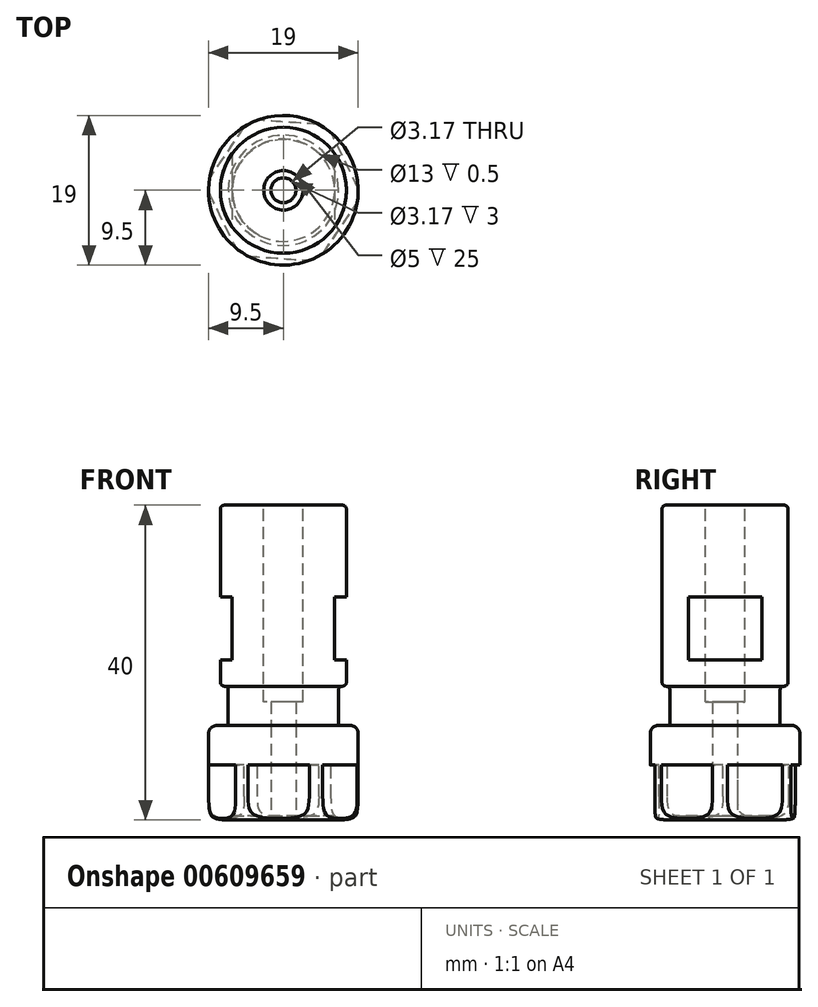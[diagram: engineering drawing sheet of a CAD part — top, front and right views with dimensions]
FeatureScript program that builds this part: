
annotation { "Feature Type Name" : "Feature", "Feature Type Description" : "" }
export const myFeature = defineFeature(function(context is Context, id is Id, definition is map)
    precondition{}
    {
        {
            var Q0;
            Q0=qCreatedBy(makeId("Top.planeOp"),FACE);
            var sketch = newSketch(context, id + "F0", { "sketchPlane" : qUnion([Q0])});
            skCircle(sketch, "E0", {"center": v(0, 0) * mm, "radius": 8 * mm});
            skSolve(sketch);
        }
        {
            var Q0;
            Q0=qSketchRegion(id+"F0",true);
            extrude(context, id + "F1", {"entities" : qUnion([Q0]), "depth" : 28 * mm, "offsetDistance" : 25 * mm});
        }
        {
            var Q0;
            Q0=qCreatedBy(makeId("Top.planeOp"),FACE);
            var sketch = newSketch(context, id + "F2", { "sketchPlane" : qUnion([Q0])});
            skCircle(sketch, "E1", {"center": v(0, 0) * mm, "radius": 7 * mm});
            skCircle(sketch, "E2", {"center": v(0, 0) * mm, "radius": 9.32 * mm});
            skSolve(sketch);
        }
        {
            var Q0;
            Q0=qSketchRegion(id+"F2",true);
            extrude(context, id + "F3", {"entities" : qUnion([Q0]), "operationType" : NewBodyOperationType.REMOVE, "depth" : 5 * mm, "offsetDistance" : 25 * mm});
        }
        {
            var Q0;
            Q0=makeQuery(id+"F1.opExtrude","CAP_FACE",FACE,{"disambiguationData":[OSD([sQuery(id+"F0.wireOp",EDGE,"E0")])],"isStart":true});
            var sketch = newSketch(context, id + "F4", { "sketchPlane" : qUnion([Q0])});
            skCircle(sketch, "E3", {"center": v(0, 0) * mm, "radius": 9.5 * mm});
            skSolve(sketch);
        }
        {
            var Q0;
            Q0=qSketchRegion(id+"F4",true);
            extrude(context, id + "F5", {"entities" : qUnion([Q0]), "depth" : 12 * mm, "offsetDistance" : 25 * mm});
        }
        {
            var Q0;
            Q0=makeQuery(id+"F5.opExtrude","CAP_FACE",FACE,{"disambiguationData":[OSD([sQuery(id+"F4.wireOp",EDGE,"E3")])],"isStart":false});
            var sketch = newSketch(context, id + "F6", { "sketchPlane" : qUnion([Q0])});
            skCircle(sketch, "E4", {"center": v(0, 0) * mm, "radius": 1.59 * mm});
            skSolve(sketch);
        }
        {
            var Q0;
            Q0=qSketchRegion(id+"F6",true);
            extrude(context, id + "F7", {"entities" : qUnion([Q0]), "operationType" : NewBodyOperationType.REMOVE, "oppositeDirection" : true, "depth" : 25 * mm, "offsetDistance" : 25 * mm});
        }
        {
            var Q0;
            Q0=makeQuery(id+"F5.opExtrude","CAP_FACE",FACE,{"disambiguationData":[OSD([sQuery(id+"F4.wireOp",EDGE,"E3")])],"isStart":false});
            var sketch = newSketch(context, id + "F8", { "sketchPlane" : qUnion([Q0])});
            skCircle(sketch, "E5.cCircle", {"center": v(0, 0) * mm, "radius": 10 * mm, "construction": true});
            skLineSegment(sketch, "E5.0", {"start": v(-5.6, 8.29) * mm, "end": v(4.38, 8.99) * mm});
            skLineSegment(sketch, "E5.1", {"start": v(4.38, 8.99) * mm, "end": v(9.98, 0.7) * mm});
            skLineSegment(sketch, "E5.2", {"start": v(9.98, 0.7) * mm, "end": v(5.6, -8.29) * mm});
            skLineSegment(sketch, "E5.3", {"start": v(5.6, -8.29) * mm, "end": v(-4.38, -8.99) * mm});
            skLineSegment(sketch, "E5.4", {"start": v(-4.38, -8.99) * mm, "end": v(-9.98, -0.7) * mm});
            skLineSegment(sketch, "E5.5", {"start": v(-9.98, -0.7) * mm, "end": v(-5.6, 8.29) * mm});
            skCircle(sketch, "E6", {"center": v(0, 0) * mm, "radius": 15.04 * mm});
            skSolve(sketch);
        }
        {
            var Q0;
            Q0=qSketchRegion(id+"F8",true);
            extrude(context, id + "F9", {"entities" : qUnion([Q0]), "operationType" : NewBodyOperationType.REMOVE, "oppositeDirection" : true, "depth" : 7 * mm, "offsetDistance" : 25 * mm});
        }
        {
            var Q0;
            Q0=makeQuery(id+"F5.opExtrude","CAP_EDGE",EDGE,{"disambiguationData":[OSD([sQuery(id+"F4.wireOp",EDGE,"E3")])],"isStart":true});
            fillet(context, id + "F10", {"entities" : qUnion([Q0]), "radius" : 1 * mm, "tangentPropagation" : true, "allowEdgeOverflow" : false});
        }
        {
            var Q0;
            {var subQ0=sQuery(id+"F4.wireOp",EDGE,"E3");Q0=makeQuery(id+"F9.boolean.opBoolean","SPLIT",EDGE,{"disambiguationData":[TD([makeQuery(id+"F5.opExtrude","SWEPT_FACE",FACE,{"disambiguationData":[OSD([subQ0])]}),makeQuery(id+"F5.opExtrude","CAP_FACE",FACE,{"disambiguationData":[OSD([subQ0])],"isStart":false}),makeQuery(id+"F9.opExtrude","SWEPT_FACE",FACE,{"disambiguationData":[OSD([sQuery(id+"F8.wireOp",EDGE,"E5.2")])]}),makeQuery(id+"F9.opExtrude","SWEPT_FACE",FACE,{"disambiguationData":[OSD([sQuery(id+"F8.wireOp",EDGE,"E5.3")])]})])],"derivedFrom":makeQuery(id+"F5.opExtrude","CAP_EDGE",EDGE,{"disambiguationData":[OSD([subQ0])],"isStart":false})});}
            fillet(context, id + "F11", {"entities" : qUnion([Q0]), "radius" : 3 * mm, "rho" : 0.7, "crossSection" : FilletCrossSection.CONIC, "allowEdgeOverflow" : false});
        }
        {
            var Q0;
            Q0=makeQuery(id+"F1.opExtrude","CAP_FACE",FACE,{"disambiguationData":[OSD([sQuery(id+"F0.wireOp",EDGE,"E0")])],"isStart":false});
            var sketch = newSketch(context, id + "F12", { "sketchPlane" : qUnion([Q0])});
            skCircle(sketch, "E7", {"center": v(0, 0) * mm, "radius": 2.5 * mm});
            skSolve(sketch);
        }
        {
            var Q0;
            Q0=qSketchRegion(id+"F12",true);
            extrude(context, id + "F13", {"entities" : qUnion([Q0]), "operationType" : NewBodyOperationType.REMOVE, "oppositeDirection" : true, "depth" : 25 * mm, "offsetDistance" : 25 * mm});
        }
        {
            var Q0;
            Q0=makeQuery(id+"F3.boolean.opBoolean","COPY",EDGE,{"derivedFrom":makeQuery(id+"F3.opExtrude","CAP_EDGE",EDGE,{"disambiguationData":[OSD([sQuery(id+"F2.wireOp",EDGE,"E1")])],"isStart":false})});
            var Q1;
            Q1=makeQuery(id+"F3.boolean.opBoolean","INTERSECT",EDGE,{"derivedFrom":[makeQuery(id+"F1.opExtrude","SWEPT_FACE",FACE,{"disambiguationData":[OSD([sQuery(id+"F0.wireOp",EDGE,"E0")])]}),makeQuery(id+"F3.opExtrude","CAP_FACE",FACE,{"disambiguationData":[OSD([sQuery(id+"F2.wireOp",EDGE,"E1"),sQuery(id+"F2.wireOp",EDGE,"E2")])],"isStart":false})]});
            var Q2;
            Q2=makeQuery(id+"F1.opExtrude","CAP_EDGE",EDGE,{"disambiguationData":[OSD([sQuery(id+"F0.wireOp",EDGE,"E0")])],"isStart":false});
            fillet(context, id + "F14", {"entities" : qUnion([Q0, Q1, Q2]), "radius" : 0.5 * mm, "tangentPropagation" : true, "allowEdgeOverflow" : false});
        }
        {
            var Q0;
            Q0=qCreatedBy(makeId("Front.planeOp"),FACE);
            var sketch = newSketch(context, id + "F15", { "sketchPlane" : qUnion([Q0])});
            skLineSegment(sketch, "E8.bottom", {"start": v(12.44, 8.34) * mm, "end": v(6.5, 8.34) * mm});
            skLineSegment(sketch, "E8.top", {"start": v(12.44, 16.34) * mm, "end": v(6.5, 16.34) * mm});
            skLineSegment(sketch, "E8.left", {"start": v(12.44, 8.34) * mm, "end": v(12.44, 16.34) * mm});
            skLineSegment(sketch, "E8.right", {"start": v(6.5, 8.34) * mm, "end": v(6.5, 16.34) * mm});
            skLineSegment(sketch, "E9", {"start": v(0, 0) * mm, "end": v(0, 36.17) * mm, "construction": true});
            skLineSegment(sketch, "E10.MirrorCS", {"start": v(-12.44, 8.34) * mm, "end": v(-6.5, 8.34) * mm});
            skLineSegment(sketch, "E11.MirrorCS", {"start": v(-12.44, 16.34) * mm, "end": v(-6.5, 16.34) * mm});
            skLineSegment(sketch, "E12.MirrorCS", {"start": v(-6.5, 8.34) * mm, "end": v(-6.5, 16.34) * mm});
            skLineSegment(sketch, "E13.MirrorCS", {"start": v(-12.44, 8.34) * mm, "end": v(-12.44, 16.34) * mm});
            skSolve(sketch);
        }
        {
            var Q0;
            Q0=qSketchRegion(id+"F15",true);
            extrude(context, id + "F16", {"entities" : qUnion([Q0]), "operationType" : NewBodyOperationType.REMOVE, "oppositeDirection" : true, "depth" : 25 * mm, "offsetDistance" : 25 * mm, "symmetric" : true});
        }
        {
            var Q0;
            Q0=makeQuery(id+"F5.opExtrude","CAP_FACE",FACE,{"disambiguationData":[OSD([sQuery(id+"F4.wireOp",EDGE,"E3")])],"isStart":false});
            extrude(context, id + "F17", {"entities" : qUnion([Q0]), "operationType" : NewBodyOperationType.REMOVE, "oppositeDirection" : true, "depth" : 0.5 * mm, "offsetDistance" : 25 * mm});
        }
    });
